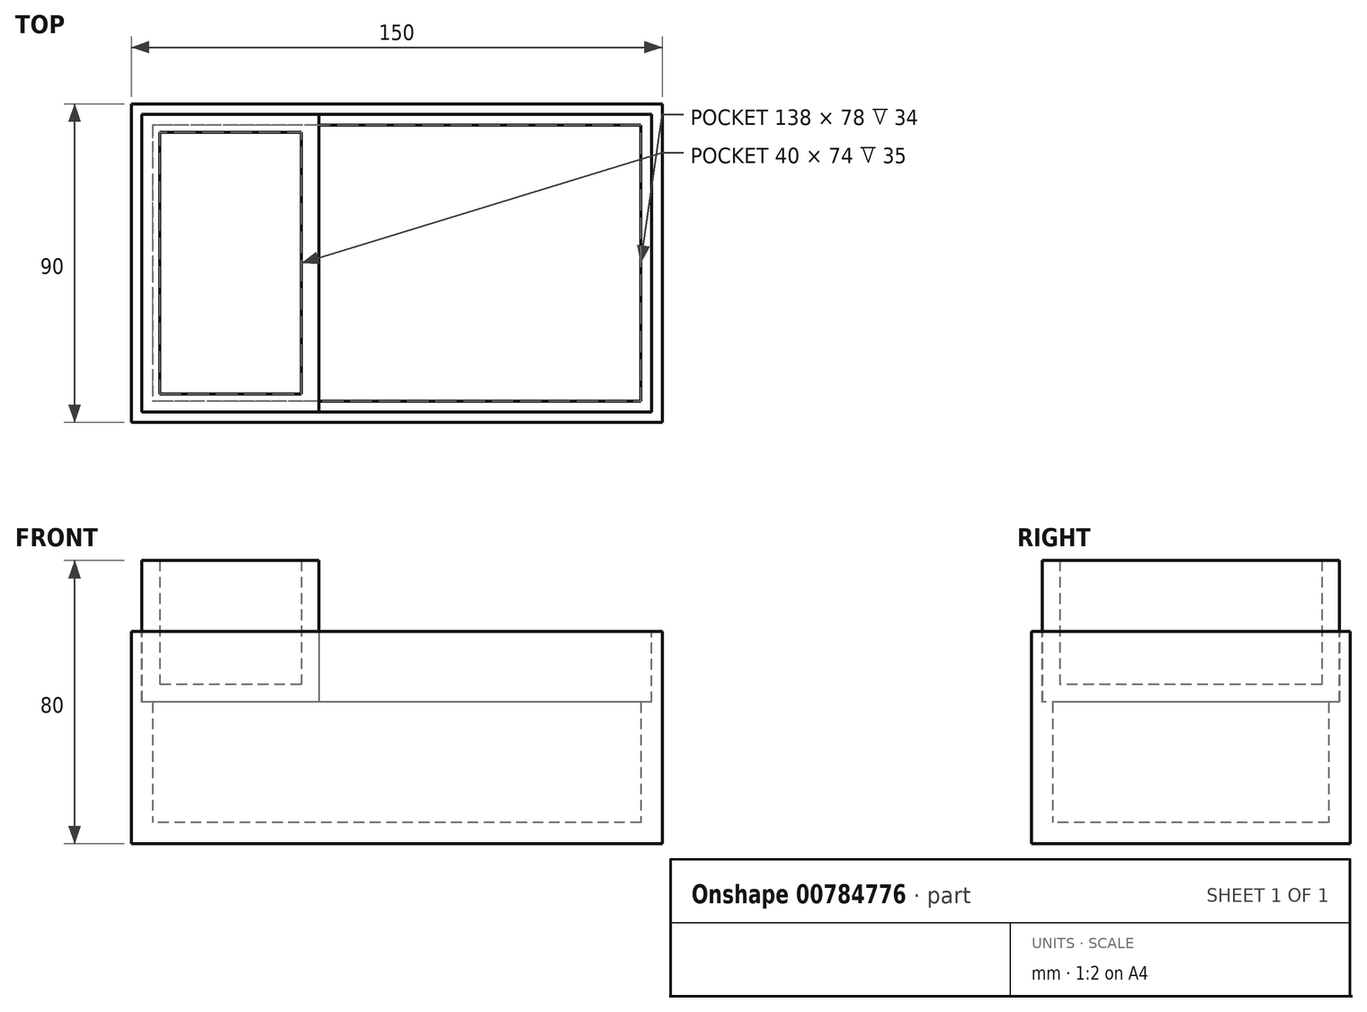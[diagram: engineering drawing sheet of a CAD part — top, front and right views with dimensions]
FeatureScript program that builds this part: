
annotation { "Feature Type Name" : "Feature", "Feature Type Description" : "" }
export const myFeature = defineFeature(function(context is Context, id is Id, definition is map)
    precondition{}
    {
        {
            var Q0;
            Q0=qCreatedBy(makeId("Top.planeOp"),FACE);
            var sketch = newSketch(context, id + "F0", { "sketchPlane" : qUnion([Q0])});
            skLineSegment(sketch, "E0.bottom", {"start": v(75, 45) * mm, "end": v(-75, 45) * mm});
            skLineSegment(sketch, "E0.top", {"start": v(75, -45) * mm, "end": v(-75, -45) * mm});
            skLineSegment(sketch, "E0.left", {"start": v(75, 45) * mm, "end": v(75, -45) * mm});
            skLineSegment(sketch, "E0.right", {"start": v(-75, 45) * mm, "end": v(-75, -45) * mm});
            skPoint(sketch, "E0.middle", {"position": v(0, 0) * mm});
            skSolve(sketch);
        }
        {
            var Q0;
            Q0 = qSketchRegion(id + "F0", true);
            extrude(context, id + "F1", {"entities" : qUnion([Q0]), "depth" : 60 * mm, "offsetDistance" : 25 * mm});
        }
        {
            var Q0;
            Q0=makeQuery(id+"F1.opExtrude","CAP_FACE",FACE,{"disambiguationData":[OSD([sQuery(id+"F0.wireOp",EDGE,"E0.bottom"),sQuery(id+"F0.wireOp",EDGE,"E0.top"),sQuery(id+"F0.wireOp",EDGE,"E0.left"),sQuery(id+"F0.wireOp",EDGE,"E0.right")])],"isStart":false});
            shell(context, id + "F2", {"entities" : qUnion([Q0]), "thickness" : 6 * mm});
        }
        {
            var Q0;
            Q0=makeQuery(id+"F1.opExtrude","CAP_FACE",FACE,{"disambiguationData":[OSD([sQuery(id+"F0.wireOp",EDGE,"E0.bottom"),sQuery(id+"F0.wireOp",EDGE,"E0.top"),sQuery(id+"F0.wireOp",EDGE,"E0.left"),sQuery(id+"F0.wireOp",EDGE,"E0.right")])],"isStart":false});
            var sketch = newSketch(context, id + "F3", { "sketchPlane" : qUnion([Q0])});
            skLineSegment(sketch, "E1.0", {"start": v(72, 42) * mm, "end": v(-72, 42) * mm});
            skLineSegment(sketch, "E1.1", {"start": v(72, 42) * mm, "end": v(72, -42) * mm});
            skLineSegment(sketch, "E1.2", {"start": v(72, -42) * mm, "end": v(-72, -42) * mm});
            skLineSegment(sketch, "E1.3", {"start": v(-72, 42) * mm, "end": v(-72, -42) * mm});
            skSolve(sketch);
        }
        {
            var Q0;
            Q0 = qSketchRegion(id + "F3", true);
            extrude(context, id + "F4", {"entities" : qUnion([Q0]), "operationType" : NewBodyOperationType.REMOVE, "oppositeDirection" : true, "depth" : 20 * mm, "offsetDistance" : 25 * mm});
        }
        {
            var Q0;
            Q0=makeQuery(id+"F4.boolean.opBoolean","COPY",FACE,{"derivedFrom":makeQuery(id+"F4.opExtrude","CAP_FACE",FACE,{"disambiguationData":[OSD([sQuery(id+"F3.wireOp",EDGE,"E1.0"),sQuery(id+"F3.wireOp",EDGE,"E1.1"),sQuery(id+"F3.wireOp",EDGE,"E1.2"),sQuery(id+"F3.wireOp",EDGE,"E1.3")])],"isStart":false})});
            var sketch = newSketch(context, id + "F5", { "sketchPlane" : qUnion([Q0])});
            skLineSegment(sketch, "E2.bottom", {"start": v(-72, 42) * mm, "end": v(-22, 42) * mm});
            skLineSegment(sketch, "E2.top", {"start": v(-72, -42) * mm, "end": v(-22, -42) * mm});
            skLineSegment(sketch, "E2.left", {"start": v(-72, 42) * mm, "end": v(-72, -42) * mm});
            skLineSegment(sketch, "E2.right", {"start": v(-22, 42) * mm, "end": v(-22, -42) * mm});
            skSolve(sketch);
        }
        {
            var Q0;
            Q0 = qSketchRegion(id + "F5", true);
            extrude(context, id + "F6", {"entities" : qUnion([Q0]), "depth" : 40 * mm, "offsetDistance" : 25 * mm});
        }
        {
            var Q0;
            Q0=makeQuery(id+"F6.opExtrude","CAP_FACE",FACE,{"disambiguationData":[OSD([sQuery(id+"F5.wireOp",EDGE,"E2.bottom"),sQuery(id+"F5.wireOp",EDGE,"E2.top"),sQuery(id+"F5.wireOp",EDGE,"E2.left"),sQuery(id+"F5.wireOp",EDGE,"E2.right")])],"isStart":false});
            shell(context, id + "F7", {"entities" : qUnion([Q0]), "thickness" : 5 * mm});
        }
    });
